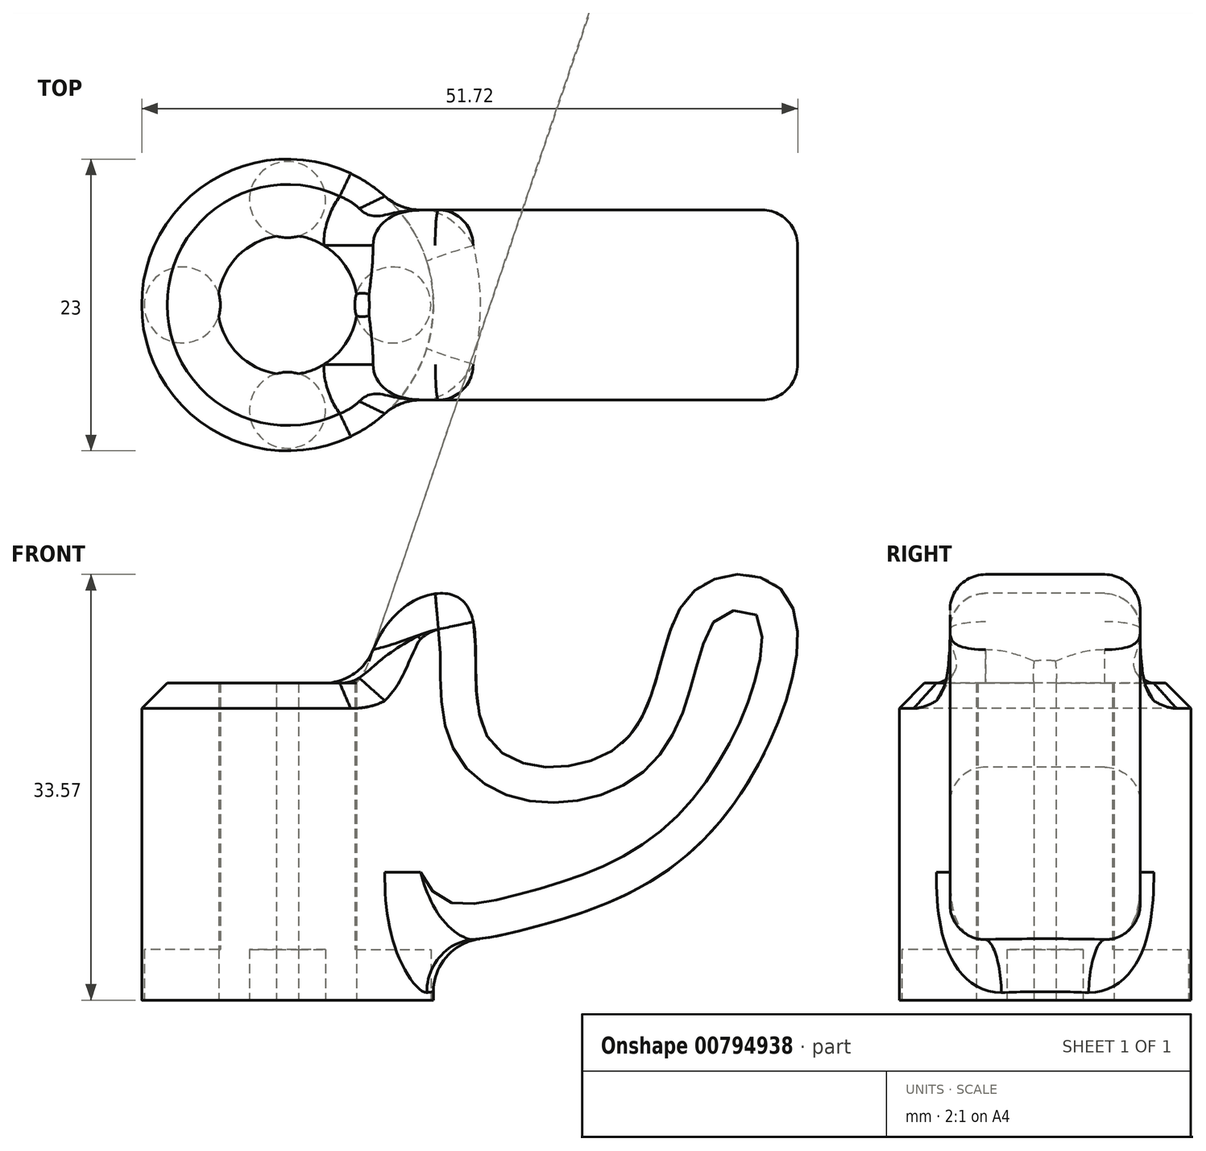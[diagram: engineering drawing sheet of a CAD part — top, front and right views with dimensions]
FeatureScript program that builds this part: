
annotation { "Feature Type Name" : "Feature", "Feature Type Description" : "" }
export const myFeature = defineFeature(function(context is Context, id is Id, definition is map)
    precondition{}
    {
        {
            var Q0;
            Q0=qCreatedBy(makeId("Top.planeOp"),FACE);
            var sketch = newSketch(context, id + "F0", { "sketchPlane" : qUnion([Q0])});
            skCircle(sketch, "E0", {"center": v(0, 0) * mm, "radius": 11.5 * mm});
            skCircle(sketch, "E1", {"center": v(0, 8.3) * mm, "radius": 3 * mm});
            skCircle(sketch, "E2.1.0", {"center": v(-8.3, 0) * mm, "radius": 3 * mm});
            skCircle(sketch, "E2.2.0", {"center": v(0, -8.3) * mm, "radius": 3 * mm});
            skCircle(sketch, "E2.3.0", {"center": v(8.3, 0) * mm, "radius": 3 * mm});
            skCircle(sketch, "E3", {"center": v(0, 0) * mm, "radius": 5.5 * mm});
            skSolve(sketch);
        }
        {
            var Q0;
            Q0=makeQuery(id+"F0.imprint","IMPRINT",FACE,{"disambiguationData":[TD([[makeQuery(id+"F0.imprint","IMPRINT",EDGE,{"derivedFrom":sQuery(id+"F0.wireOp",EDGE,"E0")}),1.0]])]});
            var Q1;
            Q1=makeQuery(id+"F0.imprint","IMPRINT",FACE,{"disambiguationData":[TD([[makeQuery(id+"F0.imprint","IMPRINT",EDGE,{"derivedFrom":sQuery(id+"F0.wireOp",EDGE,"E2.1.0")}),1.0]])]});
            var Q2;
            Q2=makeQuery(id+"F0.imprint","IMPRINT",FACE,{"disambiguationData":[TD([[makeQuery(id+"F0.imprint","IMPRINT",EDGE,{"derivedFrom":sQuery(id+"F0.wireOp",EDGE,"E1")}),1.0]])]});
            var Q3;
            Q3=makeQuery(id+"F0.imprint","IMPRINT",FACE,{"disambiguationData":[TD([[makeQuery(id+"F0.imprint","IMPRINT",EDGE,{"derivedFrom":sQuery(id+"F0.wireOp",EDGE,"E2.3.0")}),1.0]])]});
            var Q4;
            Q4=makeQuery(id+"F0.imprint","IMPRINT",FACE,{"disambiguationData":[TD([[makeQuery(id+"F0.imprint","IMPRINT",EDGE,{"derivedFrom":sQuery(id+"F0.wireOp",EDGE,"E2.2.0")}),1.0]])]});
            extrude(context, id + "F1", {"entities" : qUnion([Q0, Q1, Q2, Q3, Q4]), "depth" : 25 * mm, "offsetDistance" : 25 * mm});
        }
        {
            var Q0;
            Q0=makeQuery(id+"F0.imprint","IMPRINT",FACE,{"disambiguationData":[TD([[makeQuery(id+"F0.imprint","IMPRINT",EDGE,{"derivedFrom":sQuery(id+"F0.wireOp",EDGE,"E2.1.0")}),1.0]])]});
            var Q1;
            Q1=makeQuery(id+"F0.imprint","IMPRINT",FACE,{"disambiguationData":[TD([[makeQuery(id+"F0.imprint","IMPRINT",EDGE,{"derivedFrom":sQuery(id+"F0.wireOp",EDGE,"E2.2.0")}),1.0]])]});
            var Q2;
            Q2=makeQuery(id+"F0.imprint","IMPRINT",FACE,{"disambiguationData":[TD([[makeQuery(id+"F0.imprint","IMPRINT",EDGE,{"derivedFrom":sQuery(id+"F0.wireOp",EDGE,"E2.3.0")}),1.0]])]});
            var Q3;
            Q3=makeQuery(id+"F0.imprint","IMPRINT",FACE,{"disambiguationData":[TD([[makeQuery(id+"F0.imprint","IMPRINT",EDGE,{"derivedFrom":sQuery(id+"F0.wireOp",EDGE,"E1")}),1.0]])]});
            extrude(context, id + "F2", {"entities" : qUnion([Q0, Q1, Q2, Q3]), "operationType" : NewBodyOperationType.REMOVE, "depth" : 4 * mm, "offsetDistance" : 25 * mm});
        }
        {
            var Q0;
            Q0=qCreatedBy(makeId("Front.planeOp"),FACE);
            var sketch = newSketch(context, id + "F3", { "sketchPlane" : qUnion([Q0])});
            skFitSpline(sketch, "E4", {"points": [v(14.06, 31.23) * mm, v(15.97, 20.43) * mm, v(26.56, 20.43) * mm, v(31.85, 32.08) * mm, v(39.37, 31.86) * mm, v(33.88, 13.82) * mm, v(19.14, 5.68) * mm, v(9.32, 6.76) * mm, v(7.5, 29.11) * mm, v(14.06, 31.23) * mm]});
            skSolve(sketch);
        }
        {
            var Q0;
            Q0=makeQuery(id+"F3.imprint","IMPRINT",FACE,{"disambiguationData":[TD([[makeQuery(id+"F3.imprint","IMPRINT",EDGE,{"derivedFrom":sQuery(id+"F3.wireOp",EDGE,"E4")}),-1.0]])]});
            extrude(context, id + "F4", {"entities" : qUnion([Q0]), "operationType" : NewBodyOperationType.ADD, "endBound" : BoundingType.SYMMETRIC, "depth" : 15 * mm, "offsetDistance" : 25 * mm});
        }
        {
            var Q0;
            Q0=makeQuery(id+"F4.opExtrude","CAP_EDGE",EDGE,{"disambiguationData":[OSD([sQuery(id+"F3.wireOp",EDGE,"E4")])],"isStart":false});
            var Q1;
            Q1=makeQuery(id+"F4.opExtrude","CAP_EDGE",EDGE,{"disambiguationData":[OSD([sQuery(id+"F3.wireOp",EDGE,"E4")])],"isStart":true});
            fillet(context, id + "F5", {"entities" : qUnion([Q0, Q1]), "radius" : 2.8 * mm, "tangentPropagation" : true, "allowEdgeOverflow" : false});
        }
        {
            var Q0;
            Q0=makeQuery(id+"F4.boolean.opBoolean","INTERSECT",EDGE,{"derivedFrom":[makeQuery(id+"F1.opExtrude","CAP_FACE",FACE,{"disambiguationData":[OSD([sQuery(id+"F0.wireOp",EDGE,"E0"),sQuery(id+"F0.wireOp",EDGE,"E1"),sQuery(id+"F0.wireOp",EDGE,"E2.1.0"),sQuery(id+"F0.wireOp",EDGE,"E2.2.0"),sQuery(id+"F0.wireOp",EDGE,"E2.3.0"),sQuery(id+"F0.wireOp",EDGE,"E3")])],"isStart":false}),makeQuery(id+"F4.opExtrude","SWEPT_FACE",FACE,{"disambiguationData":[OSD([sQuery(id+"F3.wireOp",EDGE,"E4")])]})]});
            var Q1;
            Q1=makeQuery(id+"F5.opFillet","BLEND_EDGE",EDGE,{"disambiguationData":[OD(1.0)],"blendedFrom":[makeQuery(id+"F4.opExtrude","CAP_EDGE",EDGE,{"disambiguationData":[OSD([sQuery(id+"F3.wireOp",EDGE,"E4")])],"isStart":false}),makeQuery(id+"F1.opExtrude","SWEPT_FACE",FACE,{"disambiguationData":[OSD([sQuery(id+"F0.wireOp",EDGE,"E0")])]})],"blendedInto":[makeQuery(id+"F1.opExtrude","SWEPT_FACE",FACE,{"disambiguationData":[OSD([sQuery(id+"F0.wireOp",EDGE,"E0")])]})]});
            fillet(context, id + "F6", {"entities" : qUnion([Q0, Q1]), "radius" : 4.2 * mm, "tangentPropagation" : true, "allowEdgeOverflow" : false});
        }
        {
            var Q0;
            Q0=makeQuery(id+"F1.opExtrude","CAP_EDGE",EDGE,{"disambiguationData":[OSD([sQuery(id+"F0.wireOp",EDGE,"E0")])],"isStart":false});
            chamfer(context, id + "F7", {"entities" : qUnion([Q0]), "width" : 2 * mm, "tangentPropagation" : true});
        }
    });
